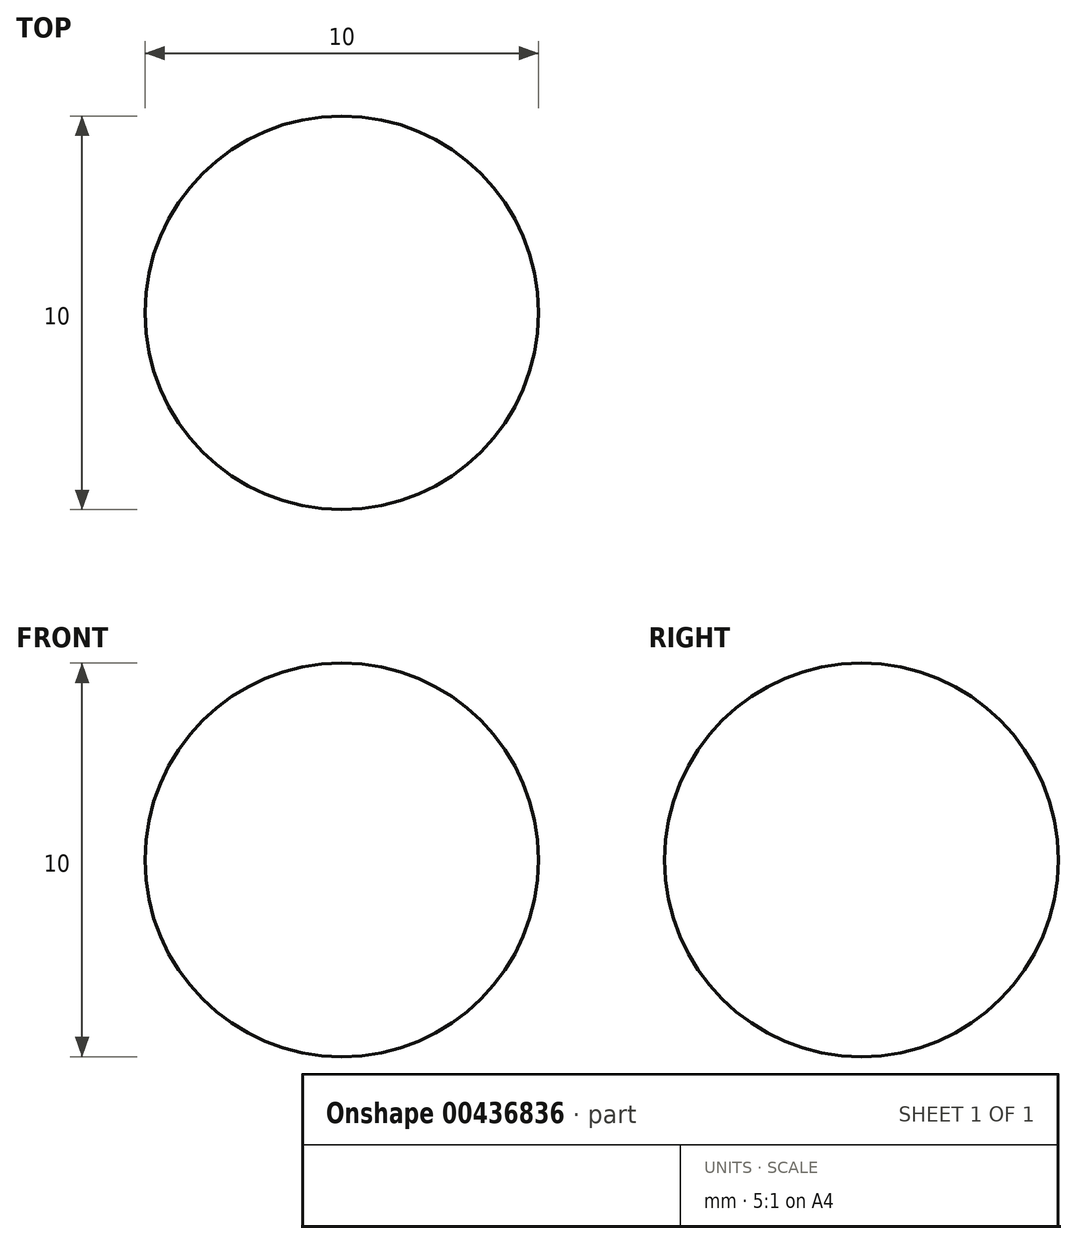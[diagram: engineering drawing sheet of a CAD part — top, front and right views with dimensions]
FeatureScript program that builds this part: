
annotation { "Feature Type Name" : "Feature", "Feature Type Description" : "" }
export const myFeature = defineFeature(function(context is Context, id is Id, definition is map)
    precondition{}
    {
        {
            var Q0;
            Q0=qCreatedBy(makeId("Front.planeOp"),FACE);
            var sketch = newSketch(context, id + "F0", { "sketchPlane" : qUnion([Q0])});
            skArc(sketch, "E0", {"start": v(0, -5) * mm, "mid": v(5, 0) * mm, "end": v(0, 5) * mm});
            skLineSegment(sketch, "E1", {"start": v(0, 5) * mm, "end": v(0, -5) * mm});
            skLineSegment(sketch, "E2", {"start": v(0, -5) * mm, "end": v(0, 5) * mm});
            skSolve(sketch);
        }
        {
            var Q0;
            Q0=makeQuery(id+"F0.imprint","IMPRINT",FACE,{"disambiguationData":[TD([[makeQuery(id+"F0.imprint","IMPRINT",EDGE,{"derivedFrom":sQuery(id+"F0.wireOp",EDGE,"E0")}),1.0]])]});
            var Q1;
            Q1=sQuery(id+"F0.wireOp",EDGE,"E2");
            revolve(context, id + "F1", {"entities" : qUnion([Q0]), "axis" : qUnion([Q1]), "revolveType" : RevolveType.FULL});
        }
    });
